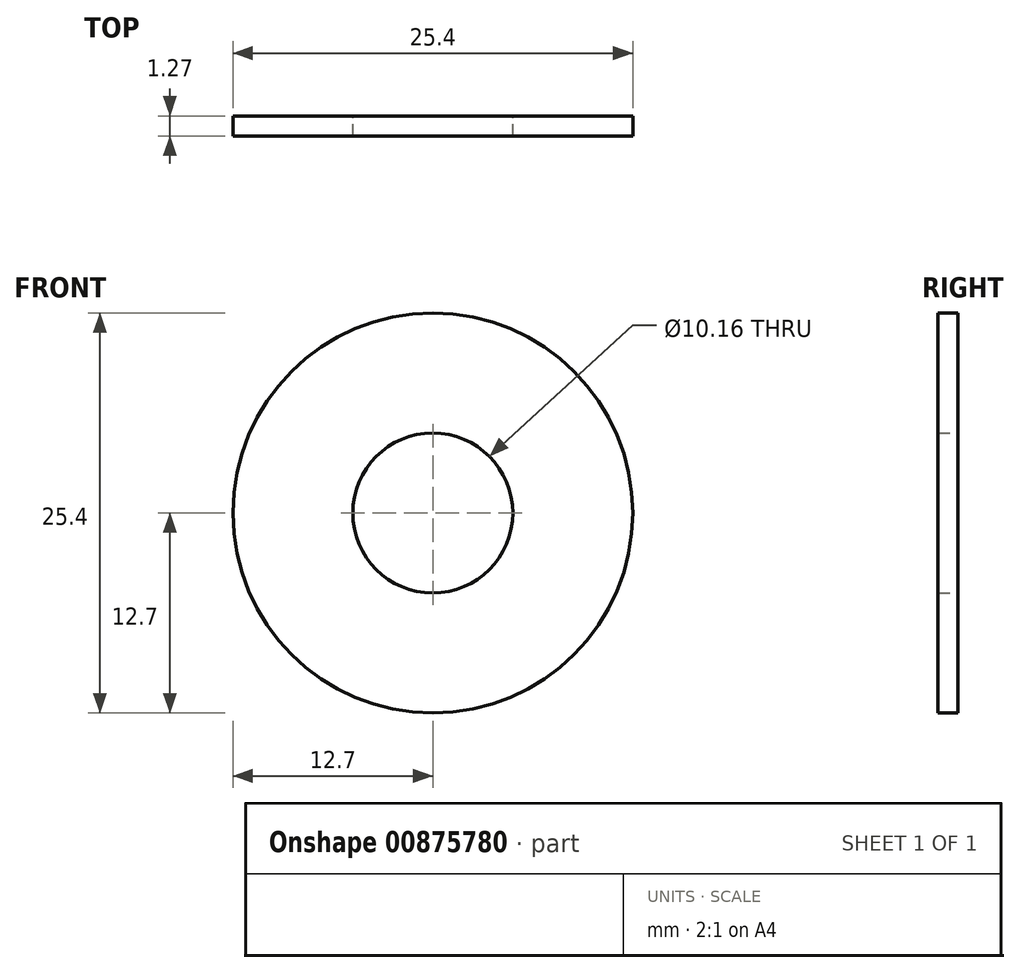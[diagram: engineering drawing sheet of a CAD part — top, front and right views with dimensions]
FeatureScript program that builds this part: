
annotation { "Feature Type Name" : "Feature", "Feature Type Description" : "" }
export const myFeature = defineFeature(function(context is Context, id is Id, definition is map)
    precondition{}
    {
        {
            var Q0;
            Q0=qCreatedBy(makeId("Front.planeOp"),FACE);
            var sketch = newSketch(context, id + "F0", { "sketchPlane" : qUnion([Q0])});
            skCircle(sketch, "E0", {"center": v(0, 0) * mm, "radius": 5.08 * mm});
            skCircle(sketch, "E1", {"center": v(0, 0) * mm, "radius": 12.7 * mm});
            skSolve(sketch);
        }
        {
            var Q0;
            Q0 = qSketchRegion(id + "F0", true);
            extrude(context, id + "F1", {"entities" : qUnion([Q0]), "depth" : 1.27 * mm, "offsetDistance" : 25.4 * mm});
        }
    });
